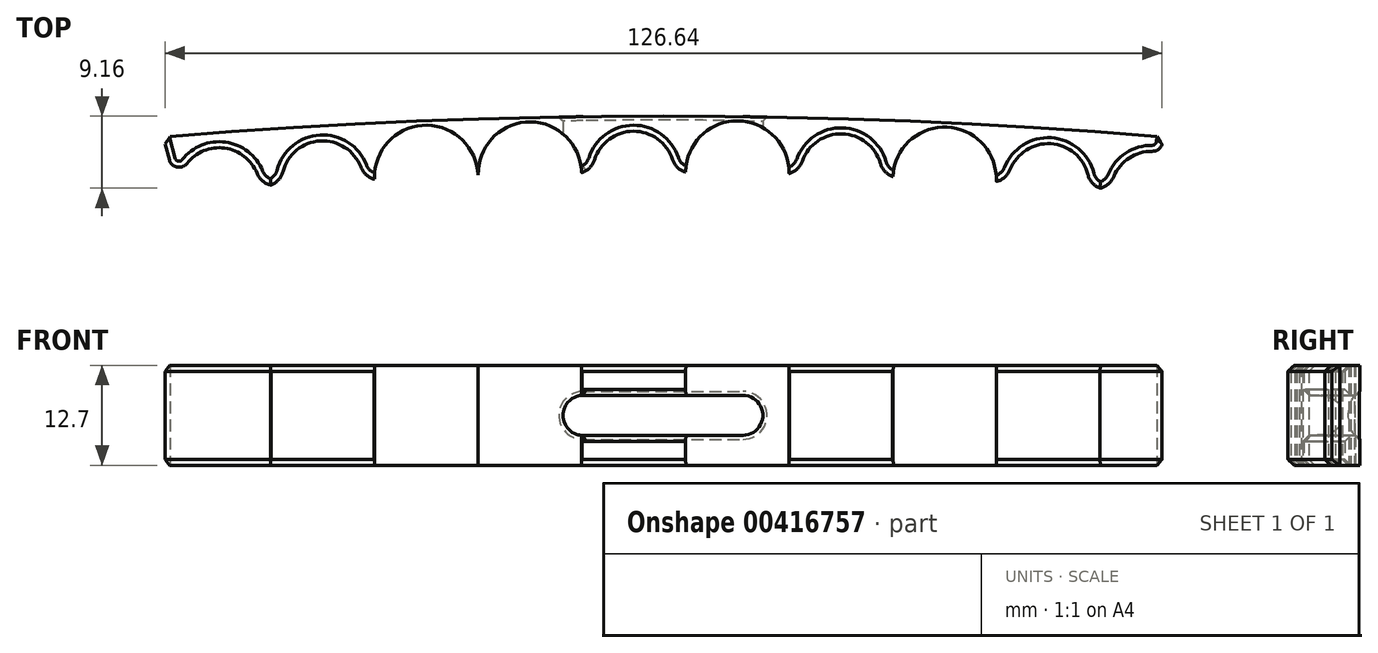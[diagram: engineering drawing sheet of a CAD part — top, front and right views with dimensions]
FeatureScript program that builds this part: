
annotation { "Feature Type Name" : "Feature", "Feature Type Description" : "" }
export const myFeature = defineFeature(function(context is Context, id is Id, definition is map)
    precondition{}
    {
        {
            var Q0;
            Q0=qCreatedBy(makeId("Top.planeOp"),FACE);
            var sketch = newSketch(context, id + "F0", { "sketchPlane" : qUnion([Q0])});
            skArc(sketch, "E0", {"start": v(63.5, 0) * mm, "mid": v(0, 2.65) * mm, "end": v(-63.5, 0) * mm});
            skLineSegment(sketch, "E1", {"start": v(63.5, 0) * mm, "end": v(-63.5, 0) * mm, "construction": true});
            skArc(sketch, "E2.0", {"start": v(62.9, -7.09) * mm, "mid": v(0, -4.46) * mm, "end": v(-62.92, -7.09) * mm});
            skLineSegment(sketch, "E3", {"start": v(-62.92, -7.09) * mm, "end": v(-63.5, 0) * mm});
            skLineSegment(sketch, "E4", {"start": v(62.9, -7.09) * mm, "end": v(63.5, 0) * mm});
            skCircle(sketch, "E5", {"center": v(-56.37, -6.57) * mm, "radius": 6.57 * mm});
            skCircle(sketch, "E6", {"center": v(-56.37, -6.57) * mm, "radius": 5.2 * mm});
            skCircle(sketch, "E7.1.0", {"center": v(-43.22, -5.7) * mm, "radius": 5.2 * mm});
            skCircle(sketch, "E7.1.1", {"center": v(-43.22, -5.7) * mm, "radius": 6.57 * mm});
            skCircle(sketch, "E7.2.0", {"center": v(-30.06, -5.06) * mm, "radius": 5.2 * mm});
            skCircle(sketch, "E7.2.1", {"center": v(-30.06, -5.06) * mm, "radius": 6.57 * mm});
            skCircle(sketch, "E7.3.0", {"center": v(-16.9, -4.65) * mm, "radius": 5.2 * mm});
            skCircle(sketch, "E7.3.1", {"center": v(-16.9, -4.65) * mm, "radius": 6.57 * mm});
            skCircle(sketch, "E7.4.0", {"center": v(-3.72, -4.47) * mm, "radius": 5.2 * mm});
            skCircle(sketch, "E7.4.1", {"center": v(-3.72, -4.47) * mm, "radius": 6.57 * mm});
            skCircle(sketch, "E7.5.0", {"center": v(9.45, -4.52) * mm, "radius": 5.2 * mm});
            skCircle(sketch, "E7.5.1", {"center": v(9.45, -4.52) * mm, "radius": 6.57 * mm});
            skCircle(sketch, "E7.6.0", {"center": v(22.63, -4.8) * mm, "radius": 5.2 * mm});
            skCircle(sketch, "E7.6.1", {"center": v(22.63, -4.8) * mm, "radius": 6.57 * mm});
            skCircle(sketch, "E7.7.0", {"center": v(35.8, -5.31) * mm, "radius": 5.2 * mm});
            skCircle(sketch, "E7.7.1", {"center": v(35.8, -5.31) * mm, "radius": 6.57 * mm});
            skCircle(sketch, "E7.8.0", {"center": v(48.94, -6.05) * mm, "radius": 5.2 * mm});
            skCircle(sketch, "E7.8.1", {"center": v(48.94, -6.05) * mm, "radius": 6.57 * mm});
            skCircle(sketch, "E7.9.0", {"center": v(62.08, -7.02) * mm, "radius": 5.2 * mm});
            skCircle(sketch, "E7.9.1", {"center": v(62.08, -7.02) * mm, "radius": 6.57 * mm});
            skLineSegment(sketch, "E7.anchor1", {"start": v(0, -759.35) * mm, "end": v(-56.37, -6.57) * mm, "construction": true});
            skLineSegment(sketch, "E7.anchor2", {"start": v(0, -759.35) * mm, "end": v(62.08, -7.02) * mm, "construction": true});
            skLineSegment(sketch, "E8", {"start": v(-61.56, -6.98) * mm, "end": v(-63.5, 0) * mm});
            skSolve(sketch);
        }
        {
            var Q0;
            {var subQ24=sQuery(id+"F0.wireOp",EDGE,"E0");Q0=makeQuery(id+"F0.imprint","IMPRINT",FACE,{"disambiguationData":[TD([[makeQuery(id+"F0.imprint","IMPRINT",EDGE,{"derivedFrom":subQ24}),1.0]])]});}
            var Q1;
            {var subQ0=sQuery(id+"F0.wireOp",EDGE,"E5");var subQ1=sQuery(id+"F0.wireOp",EDGE,"E2.0");var subQ2=makeQuery(id+"F0.imprint","INTERSECT",VERTEX,{"derivedFrom":[subQ1,subQ0]});Q1=makeQuery(id+"F0.imprint","IMPRINT",FACE,{"disambiguationData":[TD([[makeQuery(id+"F0.imprint","IMPRINT",EDGE,{"disambiguationData":[TD([[subQ2,-1.0]])],"derivedFrom":subQ1}),-1.0]])]});}
            var Q2;
            {var subQ0=sQuery(id+"F0.wireOp",EDGE,"E7.1.1");var subQ1=sQuery(id+"F0.wireOp",EDGE,"E2.0");var subQ2=makeQuery(id+"F0.imprint","INTERSECT",VERTEX,{"disambiguationData":[OD(0.0)],"derivedFrom":[subQ1,subQ0]});Q2=makeQuery(id+"F0.imprint","IMPRINT",FACE,{"disambiguationData":[TD([[makeQuery(id+"F0.imprint","IMPRINT",EDGE,{"disambiguationData":[TD([[subQ2,-1.0]])],"derivedFrom":subQ1}),-1.0]])]});}
            var Q3;
            {var subQ0=sQuery(id+"F0.wireOp",EDGE,"E7.2.1");var subQ1=sQuery(id+"F0.wireOp",EDGE,"E2.0");var subQ2=makeQuery(id+"F0.imprint","INTERSECT",VERTEX,{"disambiguationData":[OD(0.0)],"derivedFrom":[subQ1,subQ0]});Q3=makeQuery(id+"F0.imprint","IMPRINT",FACE,{"disambiguationData":[TD([[makeQuery(id+"F0.imprint","IMPRINT",EDGE,{"disambiguationData":[TD([[subQ2,-1.0]])],"derivedFrom":subQ1}),-1.0]])]});}
            var Q4;
            {var subQ0=sQuery(id+"F0.wireOp",EDGE,"E7.3.1");var subQ1=sQuery(id+"F0.wireOp",EDGE,"E2.0");var subQ2=makeQuery(id+"F0.imprint","INTERSECT",VERTEX,{"disambiguationData":[OD(0.0)],"derivedFrom":[subQ1,subQ0]});Q4=makeQuery(id+"F0.imprint","IMPRINT",FACE,{"disambiguationData":[TD([[makeQuery(id+"F0.imprint","IMPRINT",EDGE,{"disambiguationData":[TD([[subQ2,-1.0]])],"derivedFrom":subQ1}),-1.0]])]});}
            var Q5;
            {var subQ0=sQuery(id+"F0.wireOp",EDGE,"E7.4.1");var subQ1=sQuery(id+"F0.wireOp",EDGE,"E2.0");var subQ2=makeQuery(id+"F0.imprint","INTERSECT",VERTEX,{"disambiguationData":[OD(0.0)],"derivedFrom":[subQ1,subQ0]});Q5=makeQuery(id+"F0.imprint","IMPRINT",FACE,{"disambiguationData":[TD([[makeQuery(id+"F0.imprint","IMPRINT",EDGE,{"disambiguationData":[TD([[subQ2,-1.0]])],"derivedFrom":subQ1}),-1.0]])]});}
            var Q6;
            {var subQ0=sQuery(id+"F0.wireOp",EDGE,"E7.5.1");var subQ1=sQuery(id+"F0.wireOp",EDGE,"E2.0");var subQ2=makeQuery(id+"F0.imprint","INTERSECT",VERTEX,{"disambiguationData":[OD(0.0)],"derivedFrom":[subQ1,subQ0]});Q6=makeQuery(id+"F0.imprint","IMPRINT",FACE,{"disambiguationData":[TD([[makeQuery(id+"F0.imprint","IMPRINT",EDGE,{"disambiguationData":[TD([[subQ2,-1.0]])],"derivedFrom":subQ1}),-1.0]])]});}
            var Q7;
            {var subQ0=sQuery(id+"F0.wireOp",EDGE,"E7.6.1");var subQ1=sQuery(id+"F0.wireOp",EDGE,"E2.0");var subQ2=makeQuery(id+"F0.imprint","INTERSECT",VERTEX,{"disambiguationData":[OD(0.0)],"derivedFrom":[subQ1,subQ0]});Q7=makeQuery(id+"F0.imprint","IMPRINT",FACE,{"disambiguationData":[TD([[makeQuery(id+"F0.imprint","IMPRINT",EDGE,{"disambiguationData":[TD([[subQ2,-1.0]])],"derivedFrom":subQ1}),-1.0]])]});}
            var Q8;
            {var subQ0=sQuery(id+"F0.wireOp",EDGE,"E7.7.1");var subQ1=sQuery(id+"F0.wireOp",EDGE,"E2.0");var subQ2=makeQuery(id+"F0.imprint","INTERSECT",VERTEX,{"disambiguationData":[OD(0.0)],"derivedFrom":[subQ1,subQ0]});Q8=makeQuery(id+"F0.imprint","IMPRINT",FACE,{"disambiguationData":[TD([[makeQuery(id+"F0.imprint","IMPRINT",EDGE,{"disambiguationData":[TD([[subQ2,-1.0]])],"derivedFrom":subQ1}),-1.0]])]});}
            var Q9;
            {var subQ0=sQuery(id+"F0.wireOp",EDGE,"E7.8.1");var subQ1=sQuery(id+"F0.wireOp",EDGE,"E2.0");var subQ2=makeQuery(id+"F0.imprint","INTERSECT",VERTEX,{"disambiguationData":[OD(0.0)],"derivedFrom":[subQ1,subQ0]});Q9=makeQuery(id+"F0.imprint","IMPRINT",FACE,{"disambiguationData":[TD([[makeQuery(id+"F0.imprint","IMPRINT",EDGE,{"disambiguationData":[TD([[subQ2,-1.0]])],"derivedFrom":subQ1}),-1.0]])]});}
            var Q10;
            {var subQ0=sQuery(id+"F0.wireOp",EDGE,"E7.9.1");var subQ1=sQuery(id+"F0.wireOp",EDGE,"E2.0");var subQ2=makeQuery(id+"F0.imprint","INTERSECT",VERTEX,{"derivedFrom":[subQ1,subQ0]});Q10=makeQuery(id+"F0.imprint","IMPRINT",FACE,{"disambiguationData":[TD([[makeQuery(id+"F0.imprint","IMPRINT",EDGE,{"disambiguationData":[TD([[subQ2,1.0]])],"derivedFrom":subQ1}),-1.0]])]});}
            extrude(context, id + "F1", {"entities" : qUnion([Q0, Q1, Q2, Q3, Q4, Q5, Q6, Q7, Q8, Q9, Q10]), "depth" : 12.7 * mm});
        }
        {
            var Q0;
            Q0=qCreatedBy(makeId("Front.planeOp"),FACE);
            var sketch = newSketch(context, id + "F2", { "sketchPlane" : qUnion([Q0])});
            skLineSegment(sketch, "E9.0", {"start": v(63.5, 12.7) * mm, "end": v(-63.5, 12.7) * mm});
            skLineSegment(sketch, "E10.0", {"start": v(63.5, 12.7) * mm, "end": v(63.5, 0) * mm});
            skPoint(sketch, "E11.startSnap0", {"position": v(63.5, 6.35) * mm});
            skLineSegment(sketch, "E12.bottom", {"start": v(-10.16, 8.9) * mm, "end": v(10.16, 8.9) * mm});
            skLineSegment(sketch, "E12.top", {"start": v(-10.16, 3.81) * mm, "end": v(10.16, 3.81) * mm});
            skLineSegment(sketch, "E12.left", {"start": v(-12.7, 6.35) * mm, "end": v(-12.7, 6.35) * mm});
            skLineSegment(sketch, "E12.right", {"start": v(12.7, 6.35) * mm, "end": v(12.7, 6.35) * mm});
            skPoint(sketch, "E12.middle", {"position": v(0, 6.35) * mm});
            skPoint(sketch, "E13.visualSharp", {"position": v(12.7, 8.9) * mm});
            skArc(sketch, "E13.filletArc", {"start": v(12.7, 6.35) * mm, "mid": v(11.96, 8.15) * mm, "end": v(10.16, 8.9) * mm});
            skPoint(sketch, "E14.visualSharp", {"position": v(12.7, 3.81) * mm});
            skArc(sketch, "E14.filletArc", {"start": v(10.16, 3.81) * mm, "mid": v(11.96, 4.55) * mm, "end": v(12.7, 6.35) * mm});
            skPoint(sketch, "E15.visualSharp", {"position": v(-12.7, 8.9) * mm});
            skArc(sketch, "E15.filletArc", {"start": v(-10.16, 8.9) * mm, "mid": v(-11.96, 8.15) * mm, "end": v(-12.7, 6.35) * mm});
            skPoint(sketch, "E16.visualSharp", {"position": v(-12.7, 3.81) * mm});
            skArc(sketch, "E16.filletArc", {"start": v(-12.7, 6.35) * mm, "mid": v(-11.96, 4.55) * mm, "end": v(-10.16, 3.81) * mm});
            skSolve(sketch);
        }
        {
            var Q0;
            Q0=makeQuery(id+"F2.imprint","IMPRINT",FACE,{"disambiguationData":[TD([[makeQuery(id+"F2.imprint","IMPRINT",EDGE,{"derivedFrom":sQuery(id+"F2.wireOp",EDGE,"E12.bottom")}),-1.0]])]});
            extrude(context, id + "F3", {"entities" : qUnion([Q0]), "operationType" : NewBodyOperationType.REMOVE, "endBound" : BoundingType.THROUGH_ALL, "oppositeDirection" : true, "depth" : 25.4 * mm, "hasSecondDirection" : true, "secondDirectionOppositeDirection" : false, "secondDirectionDepth" : 25.4 * mm});
        }
        {
            var Q0;
            Q0=makeQuery(id+"F1.opExtrude","SWEPT_EDGE",EDGE,{"disambiguationData":[OSD([sQuery(id+"F0.wireOp",EDGE,"E2.0"),sQuery(id+"F0.wireOp",EDGE,"E7.9.0")])]});
            var Q1;
            {var subQ0=sQuery(id+"F0.wireOp",EDGE,"E7.8.0");var subQ1=sQuery(id+"F0.wireOp",EDGE,"E2.0");Q1=makeQuery(id+"F1.opExtrude","SWEPT_EDGE",EDGE,{"disambiguationData":[OSD([subQ1,subQ0]),TDD([makeQuery(id+"F0.imprint","INTERSECT",VERTEX,{"disambiguationData":[OD(0.0)],"derivedFrom":[subQ1,subQ0]})])]});}
            var Q2;
            {var subQ0=sQuery(id+"F0.wireOp",EDGE,"E7.8.0");var subQ1=sQuery(id+"F0.wireOp",EDGE,"E2.0");Q2=makeQuery(id+"F1.opExtrude","SWEPT_EDGE",EDGE,{"disambiguationData":[OSD([subQ1,subQ0]),TDD([makeQuery(id+"F0.imprint","INTERSECT",VERTEX,{"disambiguationData":[OD(1.0)],"derivedFrom":[subQ1,subQ0]})])]});}
            var Q3;
            {var subQ0=sQuery(id+"F0.wireOp",EDGE,"E7.7.0");var subQ1=sQuery(id+"F0.wireOp",EDGE,"E2.0");Q3=makeQuery(id+"F1.opExtrude","SWEPT_EDGE",EDGE,{"disambiguationData":[OSD([subQ1,subQ0]),TDD([makeQuery(id+"F0.imprint","INTERSECT",VERTEX,{"disambiguationData":[OD(0.0)],"derivedFrom":[subQ1,subQ0]})])]});}
            var Q4;
            {var subQ0=sQuery(id+"F0.wireOp",EDGE,"E7.7.0");var subQ1=sQuery(id+"F0.wireOp",EDGE,"E2.0");Q4=makeQuery(id+"F1.opExtrude","SWEPT_EDGE",EDGE,{"disambiguationData":[OSD([subQ1,subQ0]),TDD([makeQuery(id+"F0.imprint","INTERSECT",VERTEX,{"disambiguationData":[OD(1.0)],"derivedFrom":[subQ1,subQ0]})])]});}
            var Q5;
            {var subQ0=sQuery(id+"F0.wireOp",EDGE,"E7.6.0");var subQ1=sQuery(id+"F0.wireOp",EDGE,"E2.0");Q5=makeQuery(id+"F1.opExtrude","SWEPT_EDGE",EDGE,{"disambiguationData":[OSD([subQ1,subQ0]),TDD([makeQuery(id+"F0.imprint","INTERSECT",VERTEX,{"disambiguationData":[OD(0.0)],"derivedFrom":[subQ1,subQ0]})])]});}
            var Q6;
            {var subQ0=sQuery(id+"F0.wireOp",EDGE,"E7.6.0");var subQ1=sQuery(id+"F0.wireOp",EDGE,"E2.0");Q6=makeQuery(id+"F1.opExtrude","SWEPT_EDGE",EDGE,{"disambiguationData":[OSD([subQ1,subQ0]),TDD([makeQuery(id+"F0.imprint","INTERSECT",VERTEX,{"disambiguationData":[OD(1.0)],"derivedFrom":[subQ1,subQ0]})])]});}
            var Q7;
            {var subQ0=sQuery(id+"F0.wireOp",EDGE,"E7.5.0");var subQ1=sQuery(id+"F0.wireOp",EDGE,"E2.0");Q7=makeQuery(id+"F1.opExtrude","SWEPT_EDGE",EDGE,{"disambiguationData":[OSD([subQ1,subQ0]),TDD([makeQuery(id+"F0.imprint","INTERSECT",VERTEX,{"disambiguationData":[OD(0.0)],"derivedFrom":[subQ1,subQ0]})])]});}
            var Q8;
            {var subQ0=sQuery(id+"F0.wireOp",EDGE,"E7.5.0");var subQ2=sQuery(id+"F0.wireOp",EDGE,"E2.0");var subQ5=makeQuery(id+"F0.imprint","INTERSECT",VERTEX,{"disambiguationData":[OD(1.0)],"derivedFrom":[subQ2,subQ0]});Q8=makeQuery(id+"F3.boolean.opBoolean","SPLIT",EDGE,{"disambiguationData":[TD([makeQuery(id+"F3.opExtrude","SWEPT_FACE",FACE,{"disambiguationData":[OSD([sQuery(id+"F2.wireOp",EDGE,"E12.bottom")])]})])],"derivedFrom":makeQuery(id+"F1.opExtrude","SWEPT_EDGE",EDGE,{"disambiguationData":[OSD([subQ2,subQ0]),TDD([subQ5])]})});}
            var Q9;
            {var subQ0=sQuery(id+"F0.wireOp",EDGE,"E7.5.0");var subQ2=sQuery(id+"F0.wireOp",EDGE,"E2.0");var subQ5=makeQuery(id+"F0.imprint","INTERSECT",VERTEX,{"disambiguationData":[OD(1.0)],"derivedFrom":[subQ2,subQ0]});Q9=makeQuery(id+"F3.boolean.opBoolean","SPLIT",EDGE,{"disambiguationData":[TD([makeQuery(id+"F3.opExtrude","SWEPT_FACE",FACE,{"disambiguationData":[OSD([sQuery(id+"F2.wireOp",EDGE,"E12.top")])]})])],"derivedFrom":makeQuery(id+"F1.opExtrude","SWEPT_EDGE",EDGE,{"disambiguationData":[OSD([subQ2,subQ0]),TDD([subQ5])]})});}
            var Q10;
            {var subQ1=sQuery(id+"F0.wireOp",EDGE,"E7.4.0");var subQ2=sQuery(id+"F0.wireOp",EDGE,"E2.0");var subQ4=makeQuery(id+"F0.imprint","INTERSECT",VERTEX,{"disambiguationData":[OD(0.0)],"derivedFrom":[subQ2,subQ1]});Q10=makeQuery(id+"F3.boolean.opBoolean","SPLIT",EDGE,{"disambiguationData":[TD([makeQuery(id+"F3.opExtrude","SWEPT_FACE",FACE,{"disambiguationData":[OSD([sQuery(id+"F2.wireOp",EDGE,"E12.top")])]})])],"derivedFrom":makeQuery(id+"F1.opExtrude","SWEPT_EDGE",EDGE,{"disambiguationData":[OSD([subQ2,subQ1]),TDD([subQ4])]})});}
            var Q11;
            {var subQ1=sQuery(id+"F0.wireOp",EDGE,"E7.4.0");var subQ2=sQuery(id+"F0.wireOp",EDGE,"E2.0");var subQ4=makeQuery(id+"F0.imprint","INTERSECT",VERTEX,{"disambiguationData":[OD(0.0)],"derivedFrom":[subQ2,subQ1]});Q11=makeQuery(id+"F3.boolean.opBoolean","SPLIT",EDGE,{"disambiguationData":[TD([makeQuery(id+"F3.opExtrude","SWEPT_FACE",FACE,{"disambiguationData":[OSD([sQuery(id+"F2.wireOp",EDGE,"E12.bottom")])]})])],"derivedFrom":makeQuery(id+"F1.opExtrude","SWEPT_EDGE",EDGE,{"disambiguationData":[OSD([subQ2,subQ1]),TDD([subQ4])]})});}
            var Q12;
            {var subQ0=sQuery(id+"F0.wireOp",EDGE,"E7.4.0");var subQ2=sQuery(id+"F0.wireOp",EDGE,"E2.0");var subQ5=makeQuery(id+"F0.imprint","INTERSECT",VERTEX,{"disambiguationData":[OD(1.0)],"derivedFrom":[subQ2,subQ0]});Q12=makeQuery(id+"F3.boolean.opBoolean","SPLIT",EDGE,{"disambiguationData":[TD([makeQuery(id+"F3.opExtrude","SWEPT_FACE",FACE,{"disambiguationData":[OSD([sQuery(id+"F2.wireOp",EDGE,"E12.bottom")])]})])],"derivedFrom":makeQuery(id+"F1.opExtrude","SWEPT_EDGE",EDGE,{"disambiguationData":[OSD([subQ2,subQ0]),TDD([subQ5])]})});}
            var Q13;
            {var subQ0=sQuery(id+"F0.wireOp",EDGE,"E7.4.0");var subQ2=sQuery(id+"F0.wireOp",EDGE,"E2.0");var subQ5=makeQuery(id+"F0.imprint","INTERSECT",VERTEX,{"disambiguationData":[OD(1.0)],"derivedFrom":[subQ2,subQ0]});Q13=makeQuery(id+"F3.boolean.opBoolean","SPLIT",EDGE,{"disambiguationData":[TD([makeQuery(id+"F3.opExtrude","SWEPT_FACE",FACE,{"disambiguationData":[OSD([sQuery(id+"F2.wireOp",EDGE,"E12.top")])]})])],"derivedFrom":makeQuery(id+"F1.opExtrude","SWEPT_EDGE",EDGE,{"disambiguationData":[OSD([subQ2,subQ0]),TDD([subQ5])]})});}
            var Q14;
            {var subQ0=sQuery(id+"F0.wireOp",EDGE,"E7.4.0");var subQ1=sQuery(id+"F0.wireOp",EDGE,"E7.3.0");var subQ2=sQuery(id+"F0.wireOp",EDGE,"E2.0");var subQ4=makeQuery(id+"F0.imprint","INTERSECT",VERTEX,{"disambiguationData":[OD(0.0)],"derivedFrom":[subQ2,subQ1]});Q14=makeQuery(id+"F3.boolean.opBoolean","SPLIT",EDGE,{"disambiguationData":[TD([makeQuery(id+"F1.opExtrude","CAP_FACE",FACE,{"disambiguationData":[OSD([sQuery(id+"F0.wireOp",EDGE,"E0"),subQ2,sQuery(id+"F0.wireOp",EDGE,"E3"),sQuery(id+"F0.wireOp",EDGE,"E4"),sQuery(id+"F0.wireOp",EDGE,"E6"),sQuery(id+"F0.wireOp",EDGE,"E7.1.0"),sQuery(id+"F0.wireOp",EDGE,"E7.2.0"),subQ1,subQ0,sQuery(id+"F0.wireOp",EDGE,"E7.5.0"),sQuery(id+"F0.wireOp",EDGE,"E7.6.0"),sQuery(id+"F0.wireOp",EDGE,"E7.7.0"),sQuery(id+"F0.wireOp",EDGE,"E7.8.0"),sQuery(id+"F0.wireOp",EDGE,"E7.9.0")])],"isStart":true})])],"derivedFrom":makeQuery(id+"F1.opExtrude","SWEPT_EDGE",EDGE,{"disambiguationData":[OSD([subQ2,subQ1]),TDD([subQ4])]})});}
            var Q15;
            {var subQ0=sQuery(id+"F0.wireOp",EDGE,"E7.4.0");var subQ1=sQuery(id+"F0.wireOp",EDGE,"E7.3.0");var subQ2=sQuery(id+"F0.wireOp",EDGE,"E2.0");var subQ4=makeQuery(id+"F0.imprint","INTERSECT",VERTEX,{"disambiguationData":[OD(0.0)],"derivedFrom":[subQ2,subQ1]});Q15=makeQuery(id+"F3.boolean.opBoolean","SPLIT",EDGE,{"disambiguationData":[TD([makeQuery(id+"F1.opExtrude","CAP_FACE",FACE,{"disambiguationData":[OSD([sQuery(id+"F0.wireOp",EDGE,"E0"),subQ2,sQuery(id+"F0.wireOp",EDGE,"E3"),sQuery(id+"F0.wireOp",EDGE,"E4"),sQuery(id+"F0.wireOp",EDGE,"E6"),sQuery(id+"F0.wireOp",EDGE,"E7.1.0"),sQuery(id+"F0.wireOp",EDGE,"E7.2.0"),subQ1,subQ0,sQuery(id+"F0.wireOp",EDGE,"E7.5.0"),sQuery(id+"F0.wireOp",EDGE,"E7.6.0"),sQuery(id+"F0.wireOp",EDGE,"E7.7.0"),sQuery(id+"F0.wireOp",EDGE,"E7.8.0"),sQuery(id+"F0.wireOp",EDGE,"E7.9.0")])],"isStart":false})])],"derivedFrom":makeQuery(id+"F1.opExtrude","SWEPT_EDGE",EDGE,{"disambiguationData":[OSD([subQ2,subQ1]),TDD([subQ4])]})});}
            var Q16;
            {var subQ0=sQuery(id+"F0.wireOp",EDGE,"E7.3.0");var subQ1=sQuery(id+"F0.wireOp",EDGE,"E2.0");Q16=makeQuery(id+"F1.opExtrude","SWEPT_EDGE",EDGE,{"disambiguationData":[OSD([subQ1,subQ0]),TDD([makeQuery(id+"F0.imprint","INTERSECT",VERTEX,{"disambiguationData":[OD(1.0)],"derivedFrom":[subQ1,subQ0]})])]});}
            var Q17;
            {var subQ0=sQuery(id+"F0.wireOp",EDGE,"E7.2.0");var subQ1=sQuery(id+"F0.wireOp",EDGE,"E2.0");Q17=makeQuery(id+"F1.opExtrude","SWEPT_EDGE",EDGE,{"disambiguationData":[OSD([subQ1,subQ0]),TDD([makeQuery(id+"F0.imprint","INTERSECT",VERTEX,{"disambiguationData":[OD(0.0)],"derivedFrom":[subQ1,subQ0]})])]});}
            var Q18;
            {var subQ0=sQuery(id+"F0.wireOp",EDGE,"E7.2.0");var subQ1=sQuery(id+"F0.wireOp",EDGE,"E2.0");Q18=makeQuery(id+"F1.opExtrude","SWEPT_EDGE",EDGE,{"disambiguationData":[OSD([subQ1,subQ0]),TDD([makeQuery(id+"F0.imprint","INTERSECT",VERTEX,{"disambiguationData":[OD(1.0)],"derivedFrom":[subQ1,subQ0]})])]});}
            var Q19;
            {var subQ0=sQuery(id+"F0.wireOp",EDGE,"E7.1.0");var subQ1=sQuery(id+"F0.wireOp",EDGE,"E2.0");Q19=makeQuery(id+"F1.opExtrude","SWEPT_EDGE",EDGE,{"disambiguationData":[OSD([subQ1,subQ0]),TDD([makeQuery(id+"F0.imprint","INTERSECT",VERTEX,{"disambiguationData":[OD(0.0)],"derivedFrom":[subQ1,subQ0]})])]});}
            var Q20;
            {var subQ0=sQuery(id+"F0.wireOp",EDGE,"E7.1.0");var subQ1=sQuery(id+"F0.wireOp",EDGE,"E2.0");Q20=makeQuery(id+"F1.opExtrude","SWEPT_EDGE",EDGE,{"disambiguationData":[OSD([subQ1,subQ0]),TDD([makeQuery(id+"F0.imprint","INTERSECT",VERTEX,{"disambiguationData":[OD(1.0)],"derivedFrom":[subQ1,subQ0]})])]});}
            var Q21;
            {var subQ0=sQuery(id+"F0.wireOp",EDGE,"E6");var subQ1=sQuery(id+"F0.wireOp",EDGE,"E2.0");Q21=makeQuery(id+"F1.opExtrude","SWEPT_EDGE",EDGE,{"disambiguationData":[OSD([subQ1,subQ0]),TDD([makeQuery(id+"F0.imprint","INTERSECT",VERTEX,{"disambiguationData":[OD(0.0)],"derivedFrom":[subQ1,subQ0]})])]});}
            fillet(context, id + "F4", {"entities" : qUnion([Q0, Q1, Q2, Q3, Q4, Q5, Q6, Q7, Q8, Q9, Q10, Q11, Q12, Q13, Q14, Q15, Q16, Q17, Q18, Q19, Q20, Q21]), "radius" : 2.54 * mm, "tangentPropagation" : true, "allowEdgeOverflow" : false});
        }
        {
            var Q0;
            Q0=makeQuery(id+"F1.opExtrude","SWEPT_EDGE",EDGE,{"disambiguationData":[OSD([sQuery(id+"F0.wireOp",EDGE,"E2.0"),sQuery(id+"F0.wireOp",EDGE,"E6"),sQuery(id+"F0.wireOp",EDGE,"E8")])]});
            var Q1;
            Q1=makeQuery(id+"F1.opExtrude","SWEPT_EDGE",EDGE,{"disambiguationData":[OSD([sQuery(id+"F0.wireOp",EDGE,"E4"),sQuery(id+"F0.wireOp",EDGE,"E7.9.0")])]});
            fillet(context, id + "F5", {"entities" : qUnion([Q0, Q1]), "radius" : 1.27 * mm, "tangentPropagation" : true, "allowEdgeOverflow" : false});
        }
        {
            var Q0;
            Q0=makeQuery(id+"F1.opExtrude","CAP_EDGE",EDGE,{"disambiguationData":[OSD([sQuery(id+"F0.wireOp",EDGE,"E7.7.0")])],"isStart":false});
            var Q1;
            Q1=makeQuery(id+"F1.opExtrude","SWEPT_FACE",FACE,{"disambiguationData":[OSD([sQuery(id+"F0.wireOp",EDGE,"E7.9.0")])]});
            var Q2;
            Q2=makeQuery(id+"F1.opExtrude","SWEPT_FACE",FACE,{"disambiguationData":[OSD([sQuery(id+"F0.wireOp",EDGE,"E7.8.0")])]});
            var Q3;
            Q3=makeQuery(id+"F1.opExtrude","SWEPT_FACE",FACE,{"disambiguationData":[OSD([sQuery(id+"F0.wireOp",EDGE,"E7.7.0")])]});
            var Q4;
            Q4=makeQuery(id+"F1.opExtrude","SWEPT_FACE",FACE,{"disambiguationData":[OSD([sQuery(id+"F0.wireOp",EDGE,"E7.6.0")])]});
            var Q5;
            Q5=makeQuery(id+"F1.opExtrude","SWEPT_FACE",FACE,{"disambiguationData":[OSD([sQuery(id+"F0.wireOp",EDGE,"E7.5.0")])]});
            var Q6;
            {var subQ1=sQuery(id+"F0.wireOp",EDGE,"E7.4.0");Q6=makeQuery(id+"F3.boolean.opBoolean","SPLIT",FACE,{"disambiguationData":[TD([makeQuery(id+"F3.opExtrude","SWEPT_FACE",FACE,{"disambiguationData":[OSD([sQuery(id+"F2.wireOp",EDGE,"E12.top")])]})])],"derivedFrom":makeQuery(id+"F1.opExtrude","SWEPT_FACE",FACE,{"disambiguationData":[OSD([subQ1])]})});}
            var Q7;
            Q7=makeQuery(id+"F1.opExtrude","SWEPT_FACE",FACE,{"disambiguationData":[OSD([sQuery(id+"F0.wireOp",EDGE,"E7.3.0")])]});
            var Q8;
            {var subQ1=sQuery(id+"F0.wireOp",EDGE,"E7.4.0");Q8=makeQuery(id+"F3.boolean.opBoolean","SPLIT",FACE,{"disambiguationData":[TD([makeQuery(id+"F3.opExtrude","SWEPT_FACE",FACE,{"disambiguationData":[OSD([sQuery(id+"F2.wireOp",EDGE,"E12.bottom")])]})])],"derivedFrom":makeQuery(id+"F1.opExtrude","SWEPT_FACE",FACE,{"disambiguationData":[OSD([subQ1])]})});}
            var Q9;
            Q9=makeQuery(id+"F1.opExtrude","SWEPT_FACE",FACE,{"disambiguationData":[OSD([sQuery(id+"F0.wireOp",EDGE,"E7.2.0")])]});
            var Q10;
            Q10=makeQuery(id+"F1.opExtrude","SWEPT_FACE",FACE,{"disambiguationData":[OSD([sQuery(id+"F0.wireOp",EDGE,"E7.1.0")])]});
            var Q11;
            Q11=makeQuery(id+"F1.opExtrude","SWEPT_FACE",FACE,{"disambiguationData":[OSD([sQuery(id+"F0.wireOp",EDGE,"E6")])]});
            chamfer(context, id + "F6", {"entities" : qUnion([Q0, Q1, Q2, Q3, Q4, Q5, Q6, Q7, Q8, Q9, Q10, Q11]), "width" : 0.76 * mm, "tangentPropagation" : true});
        }
        {
            var Q0;
            Q0=makeQuery(id+"F3.boolean.opBoolean","INTERSECT",EDGE,{"derivedFrom":[makeQuery(id+"F1.opExtrude","SWEPT_FACE",FACE,{"disambiguationData":[OSD([sQuery(id+"F0.wireOp",EDGE,"E0")])]}),makeQuery(id+"F3.opExtrude","SWEPT_FACE",FACE,{"disambiguationData":[OSD([sQuery(id+"F2.wireOp",EDGE,"E15.filletArc"),sQuery(id+"F2.wireOp",EDGE,"E16.filletArc")])]})]});
            chamfer(context, id + "F7", {"entities" : qUnion([Q0]), "width" : 0.5 * mm, "tangentPropagation" : true});
        }
        {
            var Q0;
            Q0=makeQuery(id+"F1.opExtrude","SWEPT_EDGE",EDGE,{"disambiguationData":[OSD([sQuery(id+"F0.wireOp",EDGE,"E0"),sQuery(id+"F0.wireOp",EDGE,"E3"),sQuery(id+"F0.wireOp",EDGE,"E8")])]});
            var Q1;
            Q1=makeQuery(id+"F1.opExtrude","SWEPT_EDGE",EDGE,{"disambiguationData":[OSD([sQuery(id+"F0.wireOp",EDGE,"E0"),sQuery(id+"F0.wireOp",EDGE,"E4")])]});
            chamfer(context, id + "F8", {"entities" : qUnion([Q0, Q1]), "width" : 0.76 * mm, "tangentPropagation" : true});
        }
    });
